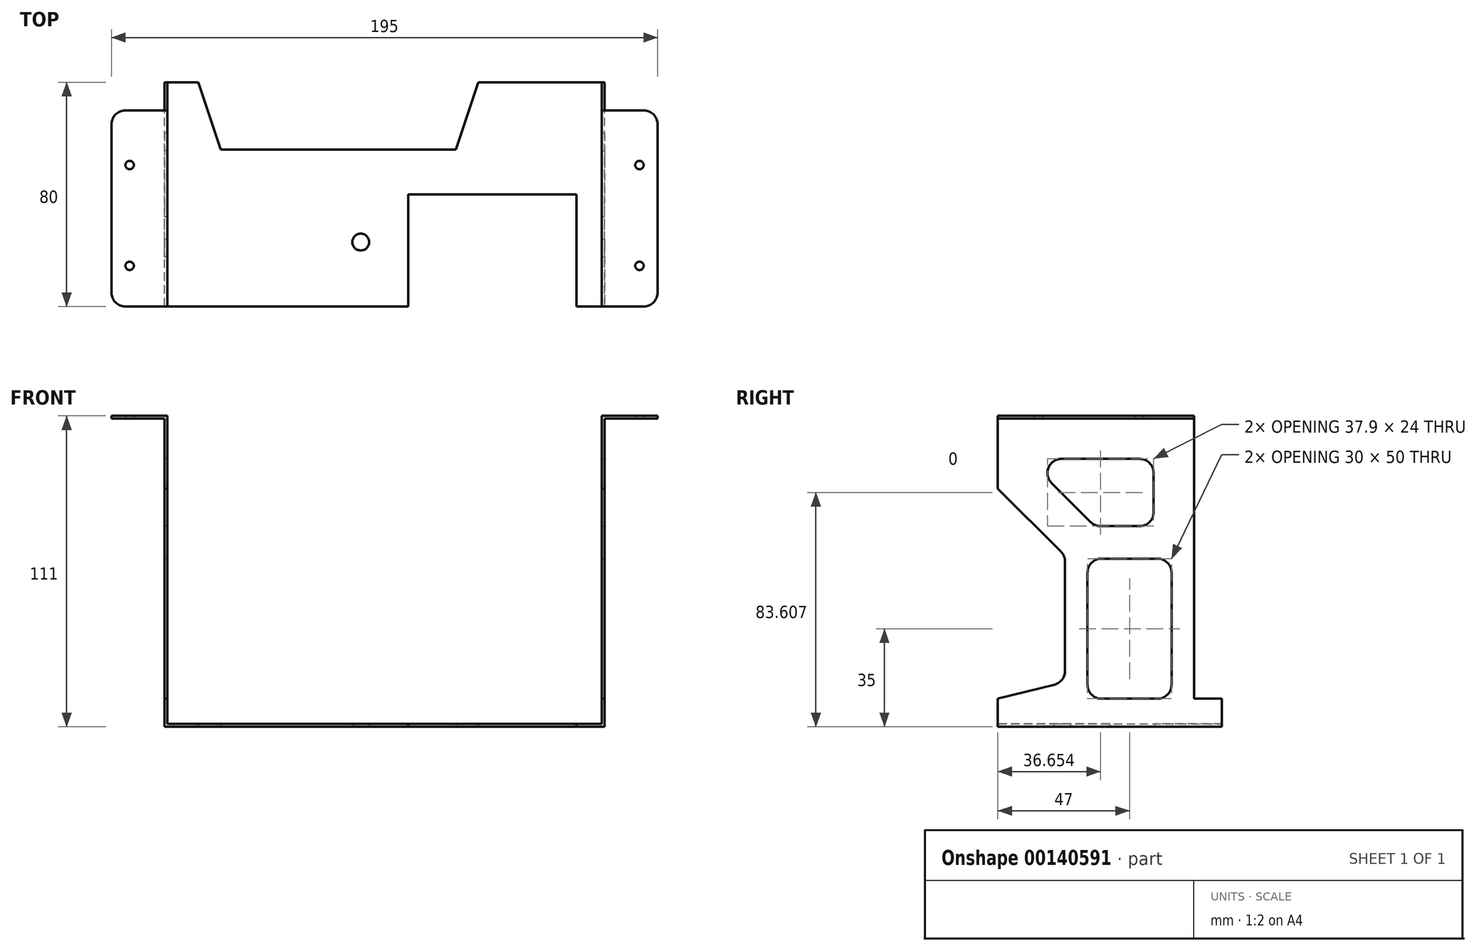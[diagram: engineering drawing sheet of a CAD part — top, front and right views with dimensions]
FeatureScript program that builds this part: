
annotation { "Feature Type Name" : "Feature", "Feature Type Description" : "" }
export const myFeature = defineFeature(function(context is Context, id is Id, definition is map)
    precondition{}
    {
        {
            var Q0;
            Q0=qCreatedBy(makeId("Top.planeOp"),FACE);
            var sketch = newSketch(context, id + "F0", { "sketchPlane" : qUnion([Q0])});
            skLineSegment(sketch, "E0.bottom", {"start": v(78.5, -40) * mm, "end": v(68.5, -40) * mm});
            skLineSegment(sketch, "E0.top", {"start": v(78.5, 40) * mm, "end": v(-78.5, 40) * mm});
            skLineSegment(sketch, "E0.left", {"start": v(78.5, -40) * mm, "end": v(78.5, 40) * mm});
            skLineSegment(sketch, "E0.right", {"start": v(-78.5, -40) * mm, "end": v(-78.5, 40) * mm});
            skPoint(sketch, "E0.middle", {"position": v(0, 0) * mm});
            skCircle(sketch, "E1", {"center": v(-8.5, -17) * mm, "radius": 3 * mm});
            skLineSegment(sketch, "E2.left", {"start": v(-66.5, 40) * mm, "end": v(-66.5, 16) * mm, "construction": true});
            skLineSegment(sketch, "E3", {"start": v(33.5, 40) * mm, "end": v(33.5, 16) * mm, "construction": true});
            skLineSegment(sketch, "E4", {"start": v(-58.5, 40) * mm, "end": v(-58.5, 16) * mm, "construction": true});
            skLineSegment(sketch, "E5", {"start": v(-58.5, 16) * mm, "end": v(-66.5, 40) * mm});
            skLineSegment(sketch, "E6", {"start": v(-58.5, 16) * mm, "end": v(25.5, 16) * mm});
            skLineSegment(sketch, "E7", {"start": v(25.5, 40) * mm, "end": v(25.5, 16) * mm, "construction": true});
            skLineSegment(sketch, "E8", {"start": v(33.5, 40) * mm, "end": v(25.5, 16) * mm});
            skLineSegment(sketch, "E9", {"start": v(25.5, 16) * mm, "end": v(-58.5, 16) * mm});
            skPoint(sketch, "E10", {"position": v(68.5, -40) * mm});
            skLineSegment(sketch, "E11", {"start": v(68.5, -40) * mm, "end": v(68.5, 0) * mm});
            skLineSegment(sketch, "E12", {"start": v(68.5, 0) * mm, "end": v(8.5, 0) * mm});
            skLineSegment(sketch, "E13", {"start": v(8.5, 0) * mm, "end": v(8.5, -40) * mm});
            skLineSegment(sketch, "E14.trimOffspring", {"start": v(8.5, -40) * mm, "end": v(-78.5, -40) * mm});
            skSolve(sketch);
        }
        {
            var Q0;
            Q0=makeQuery(id+"F0.imprint","IMPRINT",FACE,{"disambiguationData":[TD([[makeQuery(id+"F0.imprint","IMPRINT",EDGE,{"derivedFrom":sQuery(id+"F0.wireOp",EDGE,"E0.bottom")}),-1.0]])]});
            extrude(context, id + "F1", {"entities" : qUnion([Q0]), "depth" : 1 * mm});
        }
        {
            var Q0;
            Q0=makeQuery(id+"F1.opExtrude","SWEPT_FACE",FACE,{"disambiguationData":[OSD([sQuery(id+"F0.wireOp",EDGE,"E0.right")])]});
            var sketch = newSketch(context, id + "F2", { "sketchPlane" : qUnion([Q0])});
            skLineSegment(sketch, "E15.0", {"start": v(40, 0) * mm, "end": v(-40, 0) * mm});
            skLineSegment(sketch, "E16", {"start": v(40, 61) * mm, "end": v(40, 110) * mm});
            skLineSegment(sketch, "E17", {"start": v(40, 110) * mm, "end": v(-30, 110) * mm});
            skLineSegment(sketch, "E18.bottom", {"start": v(40, 85) * mm, "end": v(16, 85) * mm, "construction": true});
            skLineSegment(sketch, "E18.top", {"start": v(40, 61) * mm, "end": v(16, 61) * mm, "construction": true});
            skLineSegment(sketch, "E18.left", {"start": v(40, 85) * mm, "end": v(40, 61) * mm, "construction": true});
            skLineSegment(sketch, "E18.right", {"start": v(16, 85) * mm, "end": v(16, 61) * mm, "construction": true});
            skLineSegment(sketch, "E19", {"start": v(40, 85) * mm, "end": v(17.46, 62.46) * mm});
            skLineSegment(sketch, "E20", {"start": v(16, 58.93) * mm, "end": v(16, 19.9) * mm});
            skLineSegment(sketch, "E21", {"start": v(40, 0) * mm, "end": v(40, 10) * mm});
            skLineSegment(sketch, "E22", {"start": v(40, 10) * mm, "end": v(19.79, 15.05) * mm});
            skLineSegment(sketch, "E23", {"start": v(-40, 0) * mm, "end": v(-40, 10) * mm});
            skLineSegment(sketch, "E24", {"start": v(-40, 10) * mm, "end": v(-30, 10) * mm});
            skLineSegment(sketch, "E25", {"start": v(-30, 10) * mm, "end": v(-30, 110) * mm});
            skLineSegment(sketch, "E26.0", {"start": v(20.86, 87.07) * mm, "end": v(6.86, 73.07) * mm});
            skLineSegment(sketch, "E27", {"start": v(-15.6, 76.6) * mm, "end": v(-15.6, 90.6) * mm});
            skLineSegment(sketch, "E28", {"start": v(17.32, 95.6) * mm, "end": v(-10.6, 95.6) * mm});
            skLineSegment(sketch, "E29", {"start": v(3.32, 71.6) * mm, "end": v(-10.6, 71.6) * mm});
            skLineSegment(sketch, "E30.bottom", {"start": v(-17, 60) * mm, "end": v(3, 60) * mm});
            skLineSegment(sketch, "E30.top", {"start": v(-17, 10) * mm, "end": v(3, 10) * mm});
            skLineSegment(sketch, "E30.left", {"start": v(-22, 55) * mm, "end": v(-22, 15) * mm});
            skLineSegment(sketch, "E30.right", {"start": v(8, 55) * mm, "end": v(8, 15) * mm});
            skPoint(sketch, "E31.visualSharp", {"position": v(-15.6, 95.6) * mm});
            skArc(sketch, "E31.filletArc", {"start": v(-10.6, 95.6) * mm, "mid": v(-14.14, 94.14) * mm, "end": v(-15.6, 90.6) * mm});
            skPoint(sketch, "E32.visualSharp", {"position": v(-15.6, 71.6) * mm});
            skArc(sketch, "E32.filletArc", {"start": v(-15.6, 76.6) * mm, "mid": v(-14.14, 73.07) * mm, "end": v(-10.6, 71.6) * mm});
            skPoint(sketch, "E33.visualSharp", {"position": v(29.4, 95.6) * mm});
            skArc(sketch, "E33.filletArc", {"start": v(20.86, 87.07) * mm, "mid": v(21.94, 92.52) * mm, "end": v(17.32, 95.6) * mm});
            skPoint(sketch, "E34.visualSharp", {"position": v(8, 60) * mm});
            skArc(sketch, "E34.filletArc", {"start": v(8, 55) * mm, "mid": v(6.54, 58.54) * mm, "end": v(3, 60) * mm});
            skPoint(sketch, "E35.visualSharp", {"position": v(8, 10) * mm});
            skArc(sketch, "E35.filletArc", {"start": v(3, 10) * mm, "mid": v(6.54, 11.46) * mm, "end": v(8, 15) * mm});
            skPoint(sketch, "E36.visualSharp", {"position": v(-22, 10) * mm});
            skArc(sketch, "E36.filletArc", {"start": v(-22, 15) * mm, "mid": v(-20.54, 11.46) * mm, "end": v(-17, 10) * mm});
            skPoint(sketch, "E37.visualSharp", {"position": v(-22, 60) * mm});
            skArc(sketch, "E37.filletArc", {"start": v(-17, 60) * mm, "mid": v(-20.54, 58.54) * mm, "end": v(-22, 55) * mm});
            skPoint(sketch, "E38.visualSharp", {"position": v(5.4, 71.6) * mm});
            skArc(sketch, "E38.filletArc", {"start": v(3.32, 71.6) * mm, "mid": v(5.24, 71.99) * mm, "end": v(6.86, 73.07) * mm});
            skPoint(sketch, "E39.visualSharp", {"position": v(16, 61) * mm});
            skArc(sketch, "E39.filletArc", {"start": v(17.46, 62.46) * mm, "mid": v(16.38, 60.84) * mm, "end": v(16, 58.93) * mm});
            skPoint(sketch, "E40.visualSharp", {"position": v(16, 16) * mm});
            skArc(sketch, "E40.filletArc", {"start": v(16, 19.9) * mm, "mid": v(17.06, 16.83) * mm, "end": v(19.79, 15.05) * mm});
            skSolve(sketch);
        }
        {
            var Q0;
            {var subQ3=sQuery(id+"F2.wireOp",EDGE,"E17");Q0=makeQuery(id+"F2.imprint","IMPRINT",FACE,{"disambiguationData":[TD([[makeQuery(id+"F2.imprint","IMPRINT",EDGE,{"derivedFrom":subQ3}),1.0]])]});}
            extrude(context, id + "F3", {"entities" : qUnion([Q0]), "operationType" : NewBodyOperationType.ADD, "oppositeDirection" : true, "depth" : 1 * mm});
        }
        {
            var Q0;
            Q0=makeQuery(id+"F1.opExtrude","SWEPT_FACE",FACE,{"disambiguationData":[OSD([sQuery(id+"F0.wireOp",EDGE,"E0.left")])]});
            var sketch = newSketch(context, id + "F4", { "sketchPlane" : qUnion([Q0])});
            skLineSegment(sketch, "E41.0.0", {"start": v(40, 0) * mm, "end": v(-40, 0) * mm});
            skLineSegment(sketch, "E41.0.1", {"start": v(-40, 0) * mm, "end": v(-40, 10) * mm});
            skLineSegment(sketch, "E41.0.2", {"start": v(-40, 10) * mm, "end": v(-19.79, 15.05) * mm});
            skArc(sketch, "E41.0.3", {"start": v(-19.79, 15.05) * mm, "mid": v(-17.06, 16.83) * mm, "end": v(-16, 19.9) * mm});
            skLineSegment(sketch, "E41.0.4", {"start": v(-16, 19.9) * mm, "end": v(-16, 58.93) * mm});
            skArc(sketch, "E41.0.5", {"start": v(-16, 58.93) * mm, "mid": v(-16.38, 60.84) * mm, "end": v(-17.46, 62.46) * mm});
            skLineSegment(sketch, "E41.0.6", {"start": v(-17.46, 62.46) * mm, "end": v(-40, 85) * mm});
            skLineSegment(sketch, "E41.0.7", {"start": v(-40, 85) * mm, "end": v(-40, 110) * mm});
            skLineSegment(sketch, "E41.0.8", {"start": v(-40, 110) * mm, "end": v(30, 110) * mm});
            skLineSegment(sketch, "E41.0.9", {"start": v(30, 110) * mm, "end": v(30, 10) * mm});
            skLineSegment(sketch, "E41.0.10", {"start": v(30, 10) * mm, "end": v(40, 10) * mm});
            skLineSegment(sketch, "E41.0.11", {"start": v(40, 10) * mm, "end": v(40, 0) * mm});
            skLineSegment(sketch, "E42.0", {"start": v(-20.86, 87.07) * mm, "end": v(-6.86, 73.07) * mm});
            skArc(sketch, "E43.0", {"start": v(-20.86, 87.07) * mm, "mid": v(-21.94, 92.52) * mm, "end": v(-17.32, 95.6) * mm});
            skLineSegment(sketch, "E44.0", {"start": v(-17.32, 95.6) * mm, "end": v(10.6, 95.6) * mm});
            skArc(sketch, "E45.0", {"start": v(10.6, 95.6) * mm, "mid": v(14.14, 94.14) * mm, "end": v(15.6, 90.6) * mm});
            skLineSegment(sketch, "E46.0", {"start": v(15.6, 76.6) * mm, "end": v(15.6, 90.6) * mm});
            skArc(sketch, "E47.0", {"start": v(15.6, 76.6) * mm, "mid": v(14.14, 73.07) * mm, "end": v(10.6, 71.6) * mm});
            skLineSegment(sketch, "E48.0", {"start": v(17, 60) * mm, "end": v(-3, 60) * mm});
            skArc(sketch, "E49.0", {"start": v(-8, 55) * mm, "mid": v(-6.54, 58.54) * mm, "end": v(-3, 60) * mm});
            skLineSegment(sketch, "E50.0", {"start": v(-8, 55) * mm, "end": v(-8, 15) * mm});
            skLineSegment(sketch, "E51.0", {"start": v(-3.32, 71.6) * mm, "end": v(10.6, 71.6) * mm});
            skArc(sketch, "E52.0", {"start": v(-3.32, 71.6) * mm, "mid": v(-5.24, 71.99) * mm, "end": v(-6.86, 73.07) * mm});
            skArc(sketch, "E53.0", {"start": v(-3, 10) * mm, "mid": v(-6.54, 11.46) * mm, "end": v(-8, 15) * mm});
            skLineSegment(sketch, "E54.0", {"start": v(17, 10) * mm, "end": v(-3, 10) * mm});
            skArc(sketch, "E55.0", {"start": v(22, 15) * mm, "mid": v(20.54, 11.46) * mm, "end": v(17, 10) * mm});
            skLineSegment(sketch, "E56.0", {"start": v(22, 55) * mm, "end": v(22, 15) * mm});
            skArc(sketch, "E57.0", {"start": v(17, 60) * mm, "mid": v(20.54, 58.54) * mm, "end": v(22, 55) * mm});
            skSolve(sketch);
        }
        {
            var Q0;
            Q0 = qSketchRegion(id + "F4", true);
            extrude(context, id + "F5", {"entities" : qUnion([Q0]), "operationType" : NewBodyOperationType.ADD, "oppositeDirection" : true, "depth" : 1 * mm});
        }
        {
            var Q0;
            Q0=makeQuery(id+"F5.opExtrude","SWEPT_FACE",FACE,{"disambiguationData":[OSD([sQuery(id+"F4.wireOp",EDGE,"E41.0.8")])]});
            var sketch = newSketch(context, id + "F6", { "sketchPlane" : qUnion([Q0])});
            skLineSegment(sketch, "E58.0", {"start": v(77.5, -40) * mm, "end": v(77.5, 30) * mm});
            skLineSegment(sketch, "E59", {"start": v(77.5, 30) * mm, "end": v(92.5, 30) * mm});
            skLineSegment(sketch, "E60", {"start": v(97.5, 25) * mm, "end": v(97.5, -35) * mm});
            skLineSegment(sketch, "E61", {"start": v(92.5, -40) * mm, "end": v(77.5, -40) * mm});
            skCircle(sketch, "E62", {"center": v(91, 10.5) * mm, "radius": 1.5 * mm});
            skCircle(sketch, "E63", {"center": v(91, -25.5) * mm, "radius": 1.5 * mm});
            skPoint(sketch, "E64.visualSharp", {"position": v(97.5, 30) * mm});
            skArc(sketch, "E64.filletArc", {"start": v(97.5, 25) * mm, "mid": v(96.04, 28.54) * mm, "end": v(92.5, 30) * mm});
            skPoint(sketch, "E65.visualSharp", {"position": v(97.5, -40) * mm});
            skArc(sketch, "E65.filletArc", {"start": v(92.5, -40) * mm, "mid": v(96.04, -38.54) * mm, "end": v(97.5, -35) * mm});
            skCircle(sketch, "E66.MirrorC", {"center": v(-91, -25.5) * mm, "radius": 1.5 * mm});
            skArc(sketch, "E67.MirrorCS", {"start": v(-97.5, 25) * mm, "mid": v(-96.04, 28.54) * mm, "end": v(-92.5, 30) * mm});
            skCircle(sketch, "E68.MirrorC", {"center": v(-91, 10.5) * mm, "radius": 1.5 * mm});
            skArc(sketch, "E69.MirrorCS", {"start": v(-92.5, -40) * mm, "mid": v(-96.04, -38.54) * mm, "end": v(-97.5, -35) * mm});
            skPoint(sketch, "E70.MirrorP", {"position": v(-97.5, -40) * mm});
            skLineSegment(sketch, "E71.MirrorCS", {"start": v(-97.5, 25) * mm, "end": v(-97.5, -35) * mm});
            skLineSegment(sketch, "E72.MirrorCS", {"start": v(-77.5, 30) * mm, "end": v(-92.5, 30) * mm});
            skLineSegment(sketch, "E73.MirrorCS", {"start": v(-92.5, -40) * mm, "end": v(-77.5, -40) * mm});
            skLineSegment(sketch, "E74.MirrorCS", {"start": v(-77.5, -40) * mm, "end": v(-77.5, 30) * mm});
            skPoint(sketch, "E75.MirrorP", {"position": v(-97.5, 30) * mm});
            skSolve(sketch);
        }
        {
            var Q0;
            Q0 = qSketchRegion(id + "F6", true);
            extrude(context, id + "F7", {"entities" : qUnion([Q0]), "operationType" : NewBodyOperationType.ADD, "depth" : 1 * mm});
        }
    });
